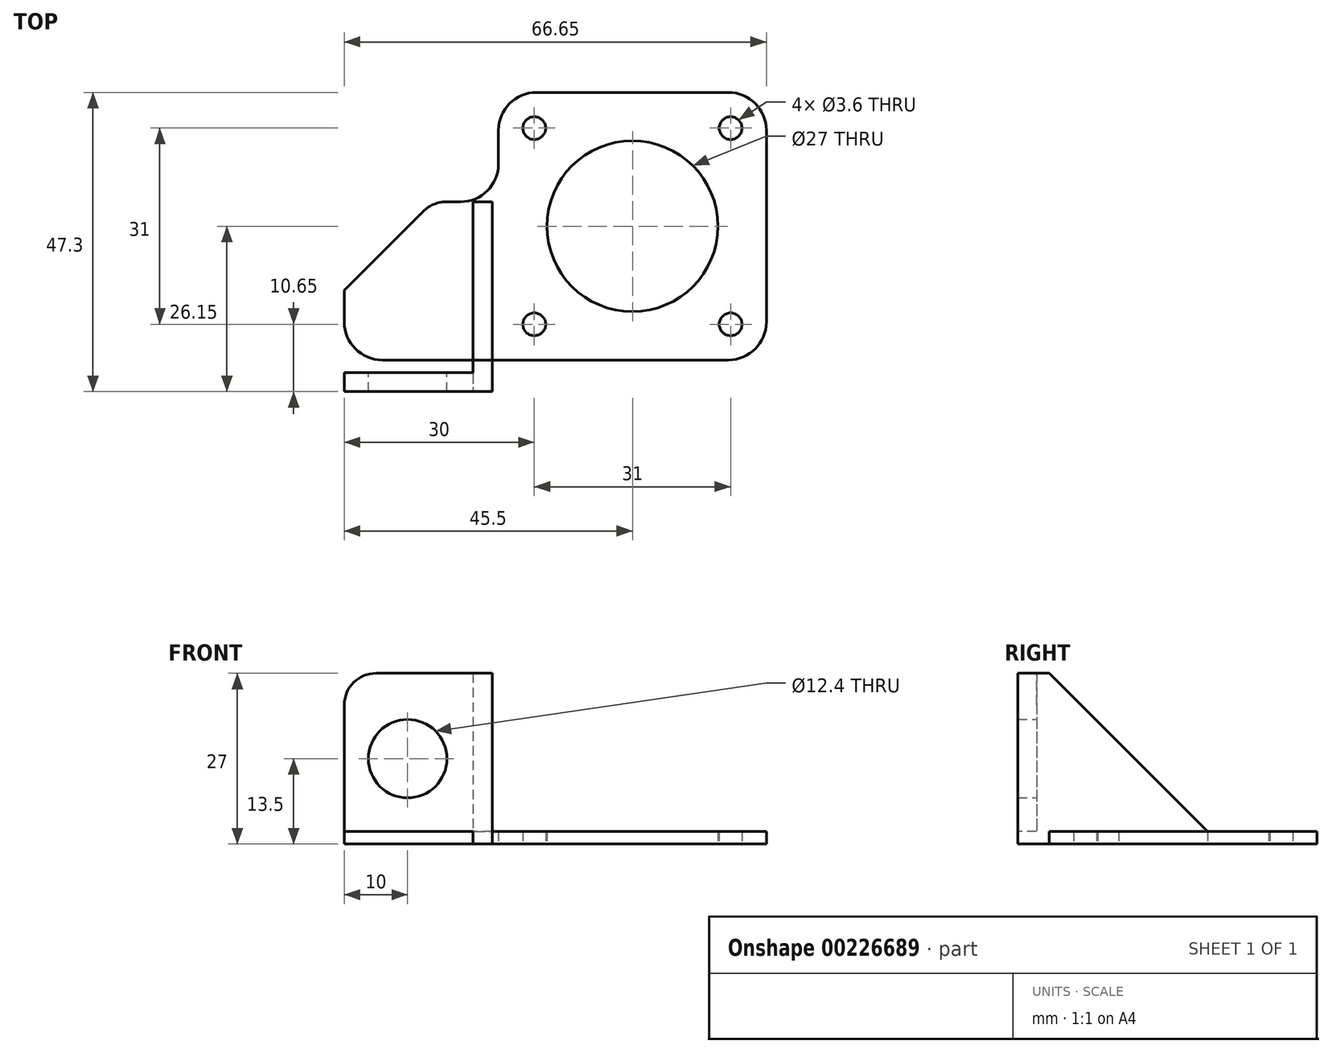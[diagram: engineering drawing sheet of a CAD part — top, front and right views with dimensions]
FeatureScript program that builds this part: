
annotation { "Feature Type Name" : "Feature", "Feature Type Description" : "" }
export const myFeature = defineFeature(function(context is Context, id is Id, definition is map)
    precondition{}
    {
        {
            var Q0;
            Q0=qCreatedBy(makeId("Top.planeOp"),FACE);
            var sketch = newSketch(context, id + "F0", { "sketchPlane" : qUnion([Q0])});
            skLineSegment(sketch, "E0.bottom", {"start": v(21.15, 21.15) * mm, "end": v(-21.15, 21.15) * mm});
            skLineSegment(sketch, "E0.top", {"start": v(21.15, -21.15) * mm, "end": v(-21.15, -21.15) * mm});
            skLineSegment(sketch, "E0.left", {"start": v(21.15, 21.15) * mm, "end": v(21.15, -21.15) * mm});
            skLineSegment(sketch, "E0.right", {"start": v(-21.15, 21.15) * mm, "end": v(-21.15, -21.15) * mm});
            skPoint(sketch, "E0.middle", {"position": v(0, 0) * mm});
            skLineSegment(sketch, "E1.bottom", {"start": v(15.5, 15.5) * mm, "end": v(-15.5, 15.5) * mm, "construction": true});
            skLineSegment(sketch, "E1.top", {"start": v(15.5, -15.5) * mm, "end": v(-15.5, -15.5) * mm, "construction": true});
            skLineSegment(sketch, "E1.left", {"start": v(15.5, 15.5) * mm, "end": v(15.5, -15.5) * mm, "construction": true});
            skLineSegment(sketch, "E1.right", {"start": v(-15.5, 15.5) * mm, "end": v(-15.5, -15.5) * mm, "construction": true});
            skCircle(sketch, "E2", {"center": v(-15.5, 15.5) * mm, "radius": 1.8 * mm});
            skCircle(sketch, "E3", {"center": v(15.5, 15.5) * mm, "radius": 1.8 * mm});
            skCircle(sketch, "E4", {"center": v(15.5, -15.5) * mm, "radius": 1.8 * mm});
            skCircle(sketch, "E5", {"center": v(-15.5, -15.5) * mm, "radius": 1.8 * mm});
            skCircle(sketch, "E6", {"center": v(0, 0) * mm, "radius": 13.5 * mm});
            skLineSegment(sketch, "E7.bottom", {"start": v(-21.15, -21.15) * mm, "end": v(-45.5, -21.15) * mm});
            skLineSegment(sketch, "E7.top", {"start": v(-21.15, 3.85) * mm, "end": v(-45.5, 3.85) * mm});
            skLineSegment(sketch, "E7.left", {"start": v(-21.15, -21.15) * mm, "end": v(-21.15, 3.85) * mm});
            skLineSegment(sketch, "E7.right", {"start": v(-45.5, -21.15) * mm, "end": v(-45.5, 3.85) * mm});
            skLineSegment(sketch, "E8.bottom", {"start": v(-45.5, -21.15) * mm, "end": v(-21.16, -21.15) * mm});
            skLineSegment(sketch, "E8.top", {"start": v(-45.5, -26.15) * mm, "end": v(-21.16, -26.15) * mm});
            skLineSegment(sketch, "E8.left", {"start": v(-45.5, -21.15) * mm, "end": v(-45.5, -26.15) * mm});
            skLineSegment(sketch, "E8.right", {"start": v(-21.16, -21.15) * mm, "end": v(-21.16, -26.15) * mm});
            skSolve(sketch);
        }
        {
            var Q0;
            Q0=makeQuery(id+"F0.imprint","IMPRINT",FACE,{"disambiguationData":[TD([[makeQuery(id+"F0.imprint","IMPRINT",EDGE,{"derivedFrom":sQuery(id+"F0.wireOp",EDGE,"E0.bottom")}),1.0]])]});
            var Q1;
            Q1=makeQuery(id+"F0.imprint","IMPRINT",FACE,{"disambiguationData":[TD([[makeQuery(id+"F0.imprint","IMPRINT",EDGE,{"derivedFrom":sQuery(id+"F0.wireOp",EDGE,"E7.bottom")}),-1.0]])]});
            var Q2;
            Q2=makeQuery(id+"F0.imprint","IMPRINT",FACE,{"disambiguationData":[TD([[makeQuery(id+"F0.imprint","IMPRINT",EDGE,{"derivedFrom":sQuery(id+"F0.wireOp",EDGE,"E8.bottom")}),-1.0]])]});
            extrude(context, id + "F1", {"entities" : qUnion([Q0, Q1, Q2]), "depth" : 2 * mm});
        }
        {
            var Q0;
            Q0=qCreatedBy(makeId("Top.planeOp"),FACE);
            var sketch = newSketch(context, id + "F2", { "sketchPlane" : qUnion([Q0])});
            skLineSegment(sketch, "E9.bottom", {"start": v(-22.16, 3.85) * mm, "end": v(-25.16, 3.85) * mm});
            skLineSegment(sketch, "E9.top", {"start": v(-22.16, -26.15) * mm, "end": v(-25.16, -26.15) * mm});
            skLineSegment(sketch, "E9.left", {"start": v(-22.16, 3.85) * mm, "end": v(-22.16, -26.15) * mm});
            skLineSegment(sketch, "E9.right", {"start": v(-25.16, 3.85) * mm, "end": v(-25.16, -26.15) * mm});
            skSolve(sketch);
        }
        {
            var Q0;
            Q0=qSketchRegion(id+"F2",true);
            extrude(context, id + "F3", {"entities" : qUnion([Q0]), "operationType" : NewBodyOperationType.ADD, "depth" : 27 * mm});
        }
        {
            var Q0;
            {var subQ0=sQuery(id+"F0.wireOp",EDGE,"E8.left");var subQ1=sQuery(id+"F0.wireOp",EDGE,"E7.right");var subQ2=sQuery(id+"F0.wireOp",EDGE,"E8.top");var subQ3=sQuery(id+"F0.wireOp",EDGE,"E7.top");Q0=makeQuery(id+"F3.boolean.opBoolean","SPLIT",FACE,{"disambiguationData":[TD([makeQuery(id+"F3.opExtrude","SWEPT_FACE",FACE,{"disambiguationData":[OSD([sQuery(id+"F2.wireOp",EDGE,"E9.right")])]})])],"derivedFrom":makeQuery(id+"F1.opExtrude","CAP_FACE",FACE,{"disambiguationData":[OSD([sQuery(id+"F0.wireOp",EDGE,"E0.bottom"),sQuery(id+"F0.wireOp",EDGE,"E0.top"),sQuery(id+"F0.wireOp",EDGE,"E0.left"),sQuery(id+"F0.wireOp",EDGE,"E0.right"),sQuery(id+"F0.wireOp",EDGE,"E2"),sQuery(id+"F0.wireOp",EDGE,"E3"),sQuery(id+"F0.wireOp",EDGE,"E4"),sQuery(id+"F0.wireOp",EDGE,"E5"),sQuery(id+"F0.wireOp",EDGE,"E6"),sQuery(id+"F0.wireOp",EDGE,"E7.bottom"),subQ3,subQ1,subQ2,subQ0,sQuery(id+"F0.wireOp",EDGE,"E8.right")])],"isStart":false})});}
            var sketch = newSketch(context, id + "F4", { "sketchPlane" : qUnion([Q0])});
            skLineSegment(sketch, "E10.bottom", {"start": v(-45.5, -23.15) * mm, "end": v(-25.16, -23.15) * mm});
            skLineSegment(sketch, "E10.top", {"start": v(-45.5, -26.15) * mm, "end": v(-25.16, -26.15) * mm});
            skLineSegment(sketch, "E10.left", {"start": v(-45.5, -23.15) * mm, "end": v(-45.5, -26.15) * mm});
            skLineSegment(sketch, "E10.right", {"start": v(-25.16, -23.15) * mm, "end": v(-25.16, -26.15) * mm});
            skSolve(sketch);
        }
        {
            var Q0;
            Q0=makeQuery(id+"F4.imprint","IMPRINT",FACE,{"disambiguationData":[TD([[makeQuery(id+"F4.imprint","IMPRINT",EDGE,{"derivedFrom":sQuery(id+"F4.wireOp",EDGE,"E10.bottom")}),-1.0]])]});
            extrude(context, id + "F5", {"entities" : qUnion([Q0]), "operationType" : NewBodyOperationType.ADD, "depth" : 25 * mm});
        }
        {
            var Q0;
            Q0=makeQuery(id+"F5.opExtrude","SWEPT_FACE",FACE,{"disambiguationData":[OSD([sQuery(id+"F4.wireOp",EDGE,"E10.bottom")])]});
            var sketch = newSketch(context, id + "F6", { "sketchPlane" : qUnion([Q0])});
            skCircle(sketch, "E11", {"center": v(35.5, 13.5) * mm, "radius": 6.2 * mm});
            skCircle(sketch, "E12", {"center": v(35.5, 13.5) * mm, "radius": 8.65 * mm, "construction": true});
            skSolve(sketch);
        }
        {
            var Q0;
            Q0=makeQuery(id+"F3.opExtrude","CAP_EDGE",EDGE,{"disambiguationData":[OSD([sQuery(id+"F2.wireOp",EDGE,"E9.bottom")])],"isStart":false});
            chamfer(context, id + "F7", {"entities" : qUnion([Q0]), "width" : 25 * mm, "tangentPropagation" : true});
        }
        {
            var Q0;
            Q0=makeQuery(id+"F1.opExtrude","SWEPT_EDGE",EDGE,{"disambiguationData":[OSD([sQuery(id+"F0.wireOp",EDGE,"E7.top"),sQuery(id+"F0.wireOp",EDGE,"E7.right")])]});
            chamfer(context, id + "F8", {"entities" : qUnion([Q0]), "width" : 14 * mm, "tangentPropagation" : true});
        }
        {
            var Q0;
            {var subQ0=sQuery(id+"F0.wireOp",EDGE,"E7.right");Q0=makeQuery(id+"F8.opChamfer","BLEND_EDGE",EDGE,{"blendedFrom":[makeQuery(id+"F1.opExtrude","SWEPT_EDGE",EDGE,{"disambiguationData":[OSD([sQuery(id+"F0.wireOp",EDGE,"E7.top"),subQ0])]}),makeQuery(id+"F5.boolean.opBoolean","MERGE",FACE,{"derivedFrom":[makeQuery(id+"F1.opExtrude","SWEPT_FACE",FACE,{"disambiguationData":[OSD([subQ0,sQuery(id+"F0.wireOp",EDGE,"E8.left")])]}),makeQuery(id+"F5.opExtrude","SWEPT_FACE",FACE,{"disambiguationData":[OSD([sQuery(id+"F4.wireOp",EDGE,"E10.left")])]})]})],"blendedInto":[makeQuery(id+"F5.boolean.opBoolean","MERGE",FACE,{"derivedFrom":[makeQuery(id+"F1.opExtrude","SWEPT_FACE",FACE,{"disambiguationData":[OSD([subQ0,sQuery(id+"F0.wireOp",EDGE,"E8.left")])]}),makeQuery(id+"F5.opExtrude","SWEPT_FACE",FACE,{"disambiguationData":[OSD([sQuery(id+"F4.wireOp",EDGE,"E10.left")])]})]})]});}
            var Q1;
            {var subQ0=sQuery(id+"F0.wireOp",EDGE,"E7.top");Q1=makeQuery(id+"F8.opChamfer","BLEND_EDGE",EDGE,{"blendedFrom":[makeQuery(id+"F1.opExtrude","SWEPT_EDGE",EDGE,{"disambiguationData":[OSD([subQ0,sQuery(id+"F0.wireOp",EDGE,"E7.right")])]}),makeQuery(id+"F3.boolean.opBoolean","MERGE",FACE,{"derivedFrom":[makeQuery(id+"F1.opExtrude","SWEPT_FACE",FACE,{"disambiguationData":[OSD([subQ0])]}),makeQuery(id+"F3.opExtrude","SWEPT_FACE",FACE,{"disambiguationData":[OSD([sQuery(id+"F2.wireOp",EDGE,"E9.bottom")])]})]})],"blendedInto":[makeQuery(id+"F3.boolean.opBoolean","MERGE",FACE,{"derivedFrom":[makeQuery(id+"F1.opExtrude","SWEPT_FACE",FACE,{"disambiguationData":[OSD([subQ0])]}),makeQuery(id+"F3.opExtrude","SWEPT_FACE",FACE,{"disambiguationData":[OSD([sQuery(id+"F2.wireOp",EDGE,"E9.bottom")])]})]})]});}
            var Q2;
            Q2=makeQuery(id+"F1.opExtrude","SWEPT_EDGE",EDGE,{"disambiguationData":[OSD([sQuery(id+"F0.wireOp",EDGE,"E8.top"),sQuery(id+"F0.wireOp",EDGE,"E8.right")])]});
            var Q3;
            Q3=makeQuery(id+"F5.opExtrude","CAP_EDGE",EDGE,{"disambiguationData":[OSD([sQuery(id+"F4.wireOp",EDGE,"E10.left")])],"isStart":false});
            fillet(context, id + "F9", {"entities" : qUnion([Q0, Q1, Q2, Q3]), "radius" : 5 * mm, "tangentPropagation" : true, "allowEdgeOverflow" : false});
        }
        {
            var Q0;
            Q0=makeQuery(id+"F1.opExtrude","SWEPT_EDGE",EDGE,{"disambiguationData":[OSD([sQuery(id+"F0.wireOp",EDGE,"E0.top"),sQuery(id+"F0.wireOp",EDGE,"E0.left")])]});
            var Q1;
            Q1=makeQuery(id+"F1.opExtrude","SWEPT_EDGE",EDGE,{"disambiguationData":[OSD([sQuery(id+"F0.wireOp",EDGE,"E0.bottom"),sQuery(id+"F0.wireOp",EDGE,"E0.left")])]});
            var Q2;
            Q2=makeQuery(id+"F1.opExtrude","SWEPT_EDGE",EDGE,{"disambiguationData":[OSD([sQuery(id+"F0.wireOp",EDGE,"E0.bottom"),sQuery(id+"F0.wireOp",EDGE,"E0.right")])]});
            var Q3;
            Q3=makeQuery(id+"F1.opExtrude","SWEPT_EDGE",EDGE,{"disambiguationData":[OSD([sQuery(id+"F0.wireOp",EDGE,"E0.right"),sQuery(id+"F0.wireOp",EDGE,"E7.top"),sQuery(id+"F0.wireOp",EDGE,"E7.left")])]});
            var Q4;
            Q4=makeQuery(id+"F1.opExtrude","SWEPT_EDGE",EDGE,{"disambiguationData":[OSD([sQuery(id+"F0.wireOp",EDGE,"E7.bottom"),sQuery(id+"F0.wireOp",EDGE,"E8.bottom"),sQuery(id+"F0.wireOp",EDGE,"E8.right")])]});
            fillet(context, id + "F10", {"entities" : qUnion([Q0, Q1, Q2, Q3, Q4]), "radius" : 6 * mm, "tangentPropagation" : true, "allowEdgeOverflow" : false});
        }
        {
            var Q0;
            Q0 = qSketchRegion(id + "F6", true);
            var Q1;
            Q1=makeQuery(id+"F5.boolean.opBoolean","MERGE",FACE,{"derivedFrom":[makeQuery(id+"F3.boolean.opBoolean","MERGE",FACE,{"derivedFrom":[makeQuery(id+"F1.opExtrude","SWEPT_FACE",FACE,{"disambiguationData":[OSD([sQuery(id+"F0.wireOp",EDGE,"E8.top")])]}),makeQuery(id+"F3.opExtrude","SWEPT_FACE",FACE,{"disambiguationData":[OSD([sQuery(id+"F2.wireOp",EDGE,"E9.top")])]})]}),makeQuery(id+"F5.opExtrude","SWEPT_FACE",FACE,{"disambiguationData":[OSD([sQuery(id+"F4.wireOp",EDGE,"E10.top")])]})]});
            extrude(context, id + "F11", {"entities" : qUnion([Q0, Q1]), "operationType" : NewBodyOperationType.REMOVE, "oppositeDirection" : true, "depth" : 25 * mm});
        }
    });
